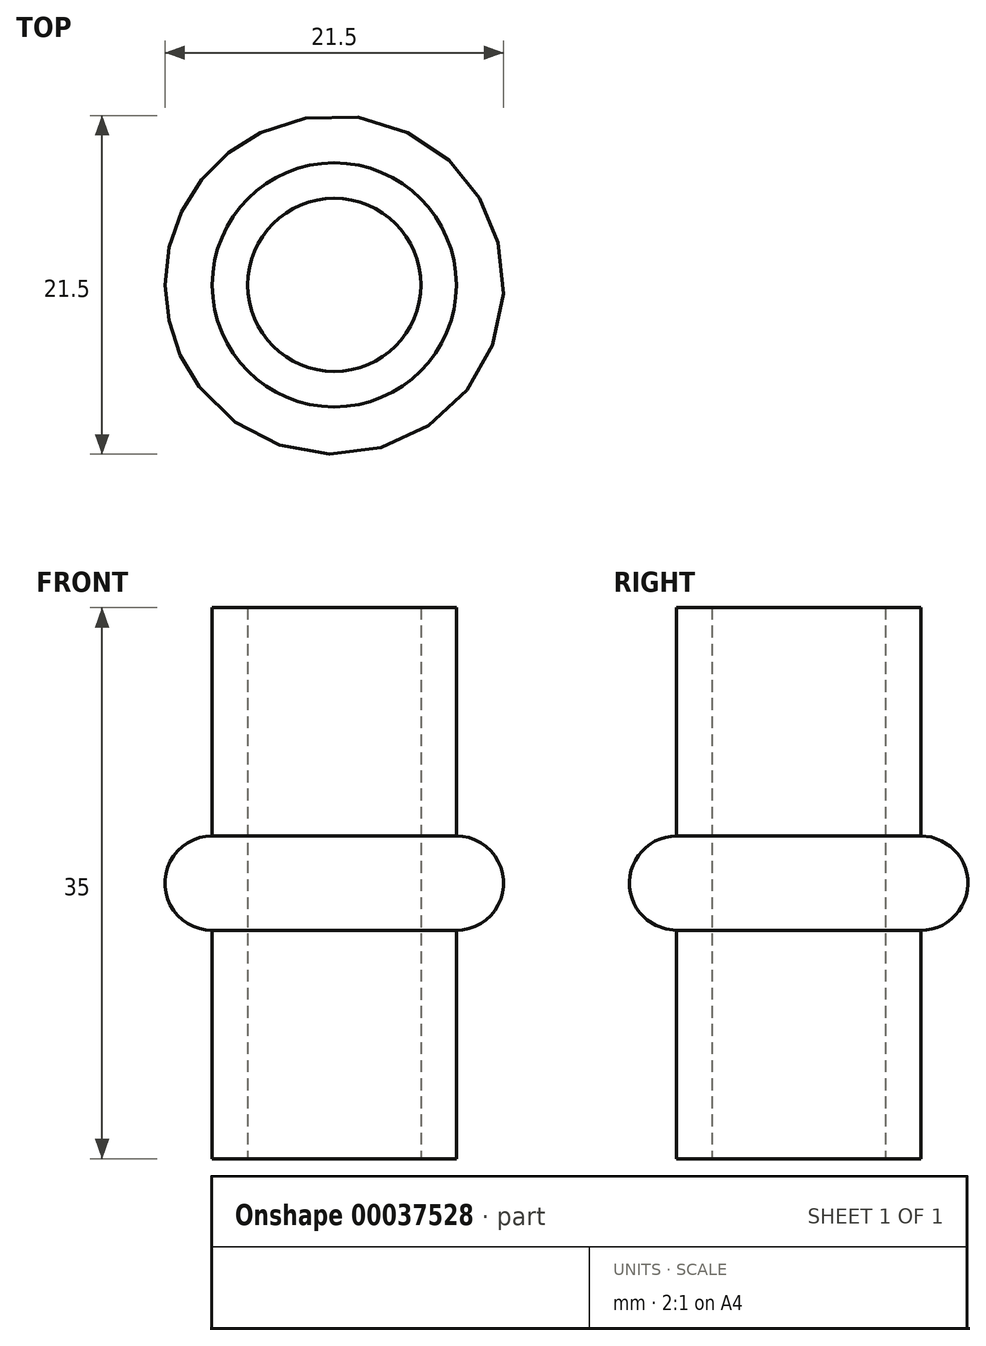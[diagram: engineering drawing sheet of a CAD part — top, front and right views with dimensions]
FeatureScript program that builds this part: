
annotation { "Feature Type Name" : "Feature", "Feature Type Description" : "" }
export const myFeature = defineFeature(function(context is Context, id is Id, definition is map)
    precondition{}
    {
        {
            var Q0;
            Q0=qCreatedBy(makeId("Top.planeOp"),FACE);
            var sketch = newSketch(context, id + "F0", { "sketchPlane" : qUnion([Q0])});
            skCircle(sketch, "E0", {"center": v(0, 0) * mm, "radius": 7.75 * mm});
            skCircle(sketch, "E1", {"center": v(0, 0) * mm, "radius": 5.5 * mm});
            skSolve(sketch);
        }
        {
            var Q0;
            Q0 = qSketchRegion(id + "F0", true);
            extrude(context, id + "F1", {"entities" : qUnion([Q0]), "depth" : 35 * mm});
        }
        {
            var Q0;
            Q0=qCreatedBy(makeId("Front.planeOp"),FACE);
            var sketch = newSketch(context, id + "F2", { "sketchPlane" : qUnion([Q0])});
            skLineSegment(sketch, "E2", {"start": v(7.75, 35) * mm, "end": v(7.75, 0) * mm});
            skPoint(sketch, "E3", {"position": v(7.75, 17.5) * mm});
            skArc(sketch, "E4", {"start": v(7.75, 14.5) * mm, "mid": v(10.75, 17.5) * mm, "end": v(7.75, 20.5) * mm});
            skLineSegment(sketch, "E5", {"start": v(0, 0) * mm, "end": v(0, 15) * mm, "construction": true});
            skSolve(sketch);
        }
        {
            var Q0;
            Q0 = qSketchRegion(id + "F2", true);
            var Q1;
            Q1=sQuery(id+"F2.wireOp",EDGE,"E5");
            revolve(context, id + "F3", {"operationType" : NewBodyOperationType.ADD, "entities" : qUnion([Q0]), "axis" : qUnion([Q1]), "revolveType" : RevolveType.FULL});
        }
    });
